# Revit family: CCMX-CORONA_PROVENCE
name_source: partatom
category: Plumbing Fixtures
units: mm (PartAtom-declared; Revit-internal decimal feet)

## family parameters
Always vertical = Yes
Cut with Voids When Loaded = No
OmniClass Number = 23.45.00.00
OmniClass Title = Sanitary, Laundry, and Cleaning Equipment
Part Type = Normal
Room Calculation Point = No
Round Connector Dimension = Use Diameter
Shared = No
Work Plane-Based = No

## types (1)
- CCMX-CORONA_PROVENCE
    Assembly Code = D2010.60
    Description = Re-interpretación de las formas clásicas añadiéndole un toque contemporáneo en sus detalles.
Agujero de rebose frontal.
    Dimensiones = https://www.ambiance.com.mx
    Ficha Tecnica = https://www.ambiance.com.mx
    Garantia de Producto = https://www.ambiance.com.mx
    Keynote = 224116
    Manual de Instalacion = https://www.ambiance.com.mx
    Manufacturer = CORONA
    Model = SERIE PROVENCE LAVAMANOS DE SOBREPONER Inspiración Atemporal
    Type Image = PROVENCE.png
    URL = https://www.ambiance.com.mx

## geometry (parser evidence)
native form markers: Sweep x3
no freeform markers — native parametric forms only
